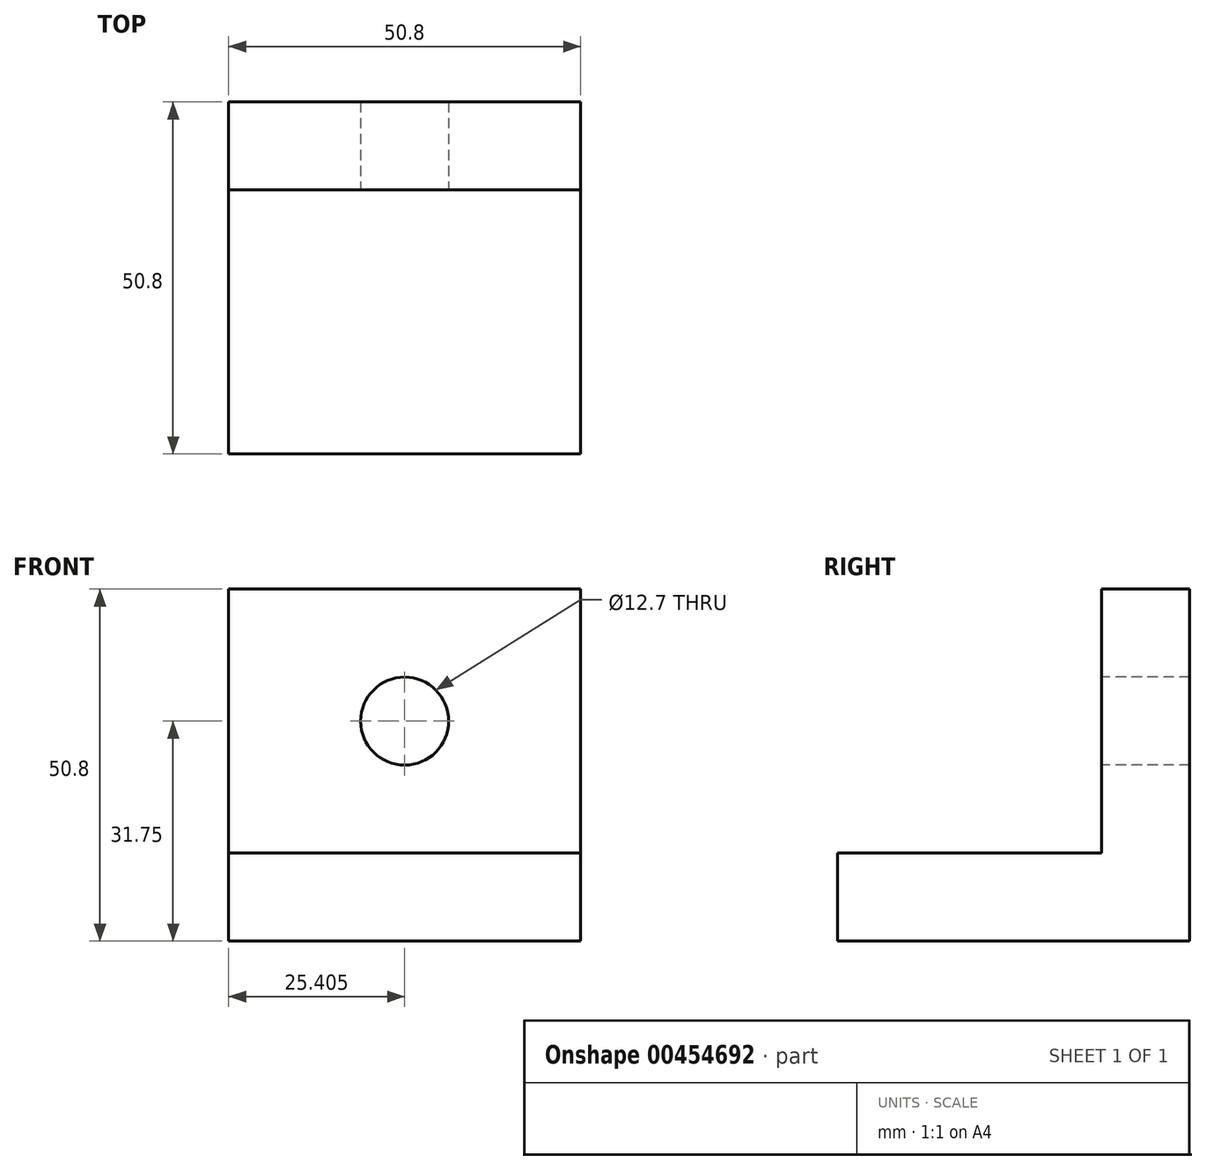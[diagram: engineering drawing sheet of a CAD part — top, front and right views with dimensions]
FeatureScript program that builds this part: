
annotation { "Feature Type Name" : "Feature", "Feature Type Description" : "" }
export const myFeature = defineFeature(function(context is Context, id is Id, definition is map)
    precondition{}
    {
        {
            var Q0;
            Q0=qCreatedBy(makeId("Top.planeOp"),FACE);
            var sketch = newSketch(context, id + "F0", { "sketchPlane" : qUnion([Q0])});
            skLineSegment(sketch, "E0.bottom", {"start": v(-27.46, 29.52) * mm, "end": v(23.34, 29.52) * mm});
            skLineSegment(sketch, "E0.top", {"start": v(-27.46, -21.28) * mm, "end": v(23.34, -21.28) * mm});
            skLineSegment(sketch, "E0.left", {"start": v(-27.46, 29.52) * mm, "end": v(-27.46, -21.28) * mm});
            skLineSegment(sketch, "E0.right", {"start": v(23.34, 29.52) * mm, "end": v(23.34, -21.28) * mm});
            skSolve(sketch);
        }
        {
            var Q0;
            Q0 = qSketchRegion(id + "F0", true);
            extrude(context, id + "F1", {"entities" : qUnion([Q0]), "depth" : 12.7 * mm});
        }
        {
            var Q0;
            Q0=makeQuery(id+"F1.opExtrude","CAP_FACE",FACE,{"disambiguationData":[OSD([sQuery(id+"F0.wireOp",EDGE,"E0.bottom"),sQuery(id+"F0.wireOp",EDGE,"E0.top"),sQuery(id+"F0.wireOp",EDGE,"E0.left"),sQuery(id+"F0.wireOp",EDGE,"E0.right")])],"isStart":false});
            var sketch = newSketch(context, id + "F2", { "sketchPlane" : qUnion([Q0])});
            skLineSegment(sketch, "E1.bottom", {"start": v(-27.46, 29.52) * mm, "end": v(23.34, 29.52) * mm});
            skLineSegment(sketch, "E1.top", {"start": v(-27.46, 16.82) * mm, "end": v(23.34, 16.82) * mm});
            skLineSegment(sketch, "E1.left", {"start": v(-27.46, 29.52) * mm, "end": v(-27.46, 16.82) * mm});
            skLineSegment(sketch, "E1.right", {"start": v(23.34, 29.52) * mm, "end": v(23.34, 16.82) * mm});
            skSolve(sketch);
        }
        {
            var Q0;
            Q0 = qSketchRegion(id + "F2", true);
            extrude(context, id + "F3", {"entities" : qUnion([Q0]), "operationType" : NewBodyOperationType.ADD, "depth" : 38.1 * mm});
        }
        {
            var Q0;
            Q0=makeQuery(id+"F3.opExtrude","SWEPT_FACE",FACE,{"disambiguationData":[OSD([sQuery(id+"F2.wireOp",EDGE,"E1.top")])]});
            var sketch = newSketch(context, id + "F4", { "sketchPlane" : qUnion([Q0])});
            skLineSegment(sketch, "E2", {"start": v(0, 50.8) * mm, "end": v(-2.06, 50.8) * mm});
            skCircle(sketch, "E3", {"center": v(-2.06, 31.75) * mm, "radius": 6.35 * mm});
            skSolve(sketch);
        }
        {
            var Q0;
            Q0 = qSketchRegion(id + "F4", true);
            extrude(context, id + "F5", {"entities" : qUnion([Q0]), "operationType" : NewBodyOperationType.REMOVE, "oppositeDirection" : true, "depth" : 25.4 * mm});
        }
    });
